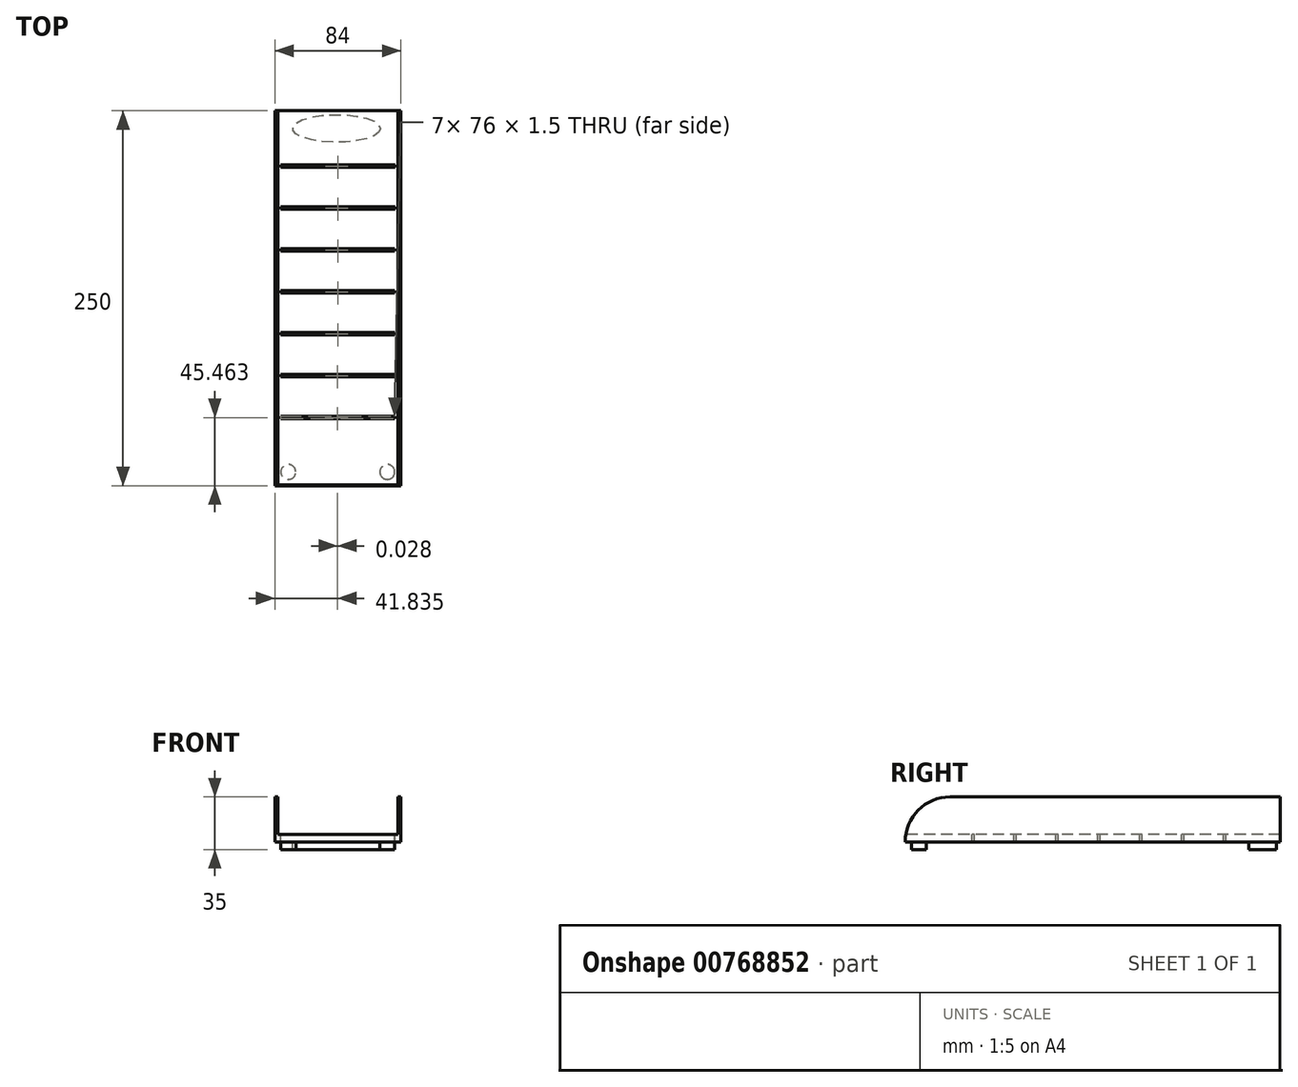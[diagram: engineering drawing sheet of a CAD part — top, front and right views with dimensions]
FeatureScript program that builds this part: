
annotation { "Feature Type Name" : "Feature", "Feature Type Description" : "" }
export const myFeature = defineFeature(function(context is Context, id is Id, definition is map)
    precondition{}
    {
        {
            var Q0;
            Q0=qCreatedBy(makeId("Front.planeOp"),FACE);
            var sketch = newSketch(context, id + "F0", { "sketchPlane" : qUnion([Q0])});
            skLineSegment(sketch, "E0.bottom", {"start": v(0, 0) * mm, "end": v(-84, 0) * mm});
            skLineSegment(sketch, "E0.top", {"start": v(0, 30) * mm, "end": v(-84, 30) * mm});
            skLineSegment(sketch, "E0.left", {"start": v(0, 0) * mm, "end": v(0, 30) * mm});
            skLineSegment(sketch, "E0.right", {"start": v(-84, 0) * mm, "end": v(-84, 30) * mm});
            skSolve(sketch);
        }
        {
            var Q0;
            Q0 = qSketchRegion(id + "F0", true);
            extrude(context, id + "F1", {"entities" : qUnion([Q0]), "oppositeDirection" : true, "depth" : 250 * mm, "offsetDistance" : 25.4 * mm});
        }
        {
            var Q0;
            Q0=qCreatedBy(makeId("Front.planeOp"),FACE);
            var sketch = newSketch(context, id + "F2", { "sketchPlane" : qUnion([Q0])});
            skLineSegment(sketch, "E1.bottom", {"start": v(-82, 55.6) * mm, "end": v(-2, 55.6) * mm});
            skLineSegment(sketch, "E1.top", {"start": v(-82, 5) * mm, "end": v(-2, 5) * mm});
            skLineSegment(sketch, "E1.left", {"start": v(-82, 55.6) * mm, "end": v(-82, 5) * mm});
            skLineSegment(sketch, "E1.right", {"start": v(-2, 55.6) * mm, "end": v(-2, 5) * mm});
            skSolve(sketch);
        }
        {
            var Q0;
            Q0=makeQuery(id+"F2.imprint","IMPRINT",FACE,{"disambiguationData":[TD([[makeQuery(id+"F2.imprint","IMPRINT",EDGE,{"derivedFrom":sQuery(id+"F2.wireOp",EDGE,"E1.bottom")}),-1.0]])]});
            extrude(context, id + "F3", {"entities" : qUnion([Q0]), "operationType" : NewBodyOperationType.REMOVE, "endBound" : BoundingType.THROUGH_ALL, "oppositeDirection" : true, "depth" : 25.4 * mm, "offsetDistance" : 25.4 * mm});
        }
        {
            var Q0;
            Q0=makeQuery(id+"F1.opExtrude","SWEPT_FACE",FACE,{"disambiguationData":[OSD([sQuery(id+"F0.wireOp",EDGE,"E0.bottom")])]});
            var sketch = newSketch(context, id + "F4", { "sketchPlane" : qUnion([Q0])});
            skCircle(sketch, "E2", {"center": v(-75.07, -9.18) * mm, "radius": 5 * mm});
            skEllipse(sketch, "E3", {"center": v(-42.93, -238.18) * mm, "majorRadius": 29.27 * mm, "minorRadius": 9.21 * mm, "majorAxis": v(1, 0)});
            skPoint(sketch, "E4.0.internal.snap0", {"position": v(-42, 0) * mm});
            skPoint(sketch, "E4.1.internal.snap0", {"position": v(-42, 0) * mm});
            skPoint(sketch, "E4.2.internal.snap0", {"position": v(-42, 0) * mm});
            skFitSpline(sketch, "E4", {"points": [v(-42, 9.43) * mm, v(-42, -255.98) * mm, v(-42, -257.6) * mm], "startDerivative": vector(0, -408.49) * mm, "endDerivative": vector(0, -12.81) * mm});
            skCircle(sketch, "E5.1.0.0", {"center": v(-9.07, -9.18) * mm, "radius": 5 * mm});
            skLineSegment(sketch, "E5.direction1", {"start": v(-75.07, -9.18) * mm, "end": v(-9.07, -9.18) * mm, "construction": true});
            skSolve(sketch);
        }
        {
            var Q0;
            Q0=makeQuery(id+"F4.imprint","IMPRINT",FACE,{"disambiguationData":[TD([[makeQuery(id+"F4.imprint","IMPRINT",EDGE,{"derivedFrom":sQuery(id+"F4.wireOp",EDGE,"E2")}),1.0]])]});
            var Q1;
            Q1=makeQuery(id+"F4.imprint","IMPRINT",FACE,{"disambiguationData":[TD([[makeQuery(id+"F4.imprint","IMPRINT",EDGE,{"derivedFrom":sQuery(id+"F4.wireOp",EDGE,"E5.1.0.0")}),1.0]])]});
            var Q2;
            {var subQ0=sQuery(id+"F4.wireOp",EDGE,"E4");var subQ1=sQuery(id+"F4.wireOp",EDGE,"E3");var subQ2=makeQuery(id+"F4.imprint","INTERSECT",VERTEX,{"disambiguationData":[OD(0.0)],"derivedFrom":[subQ1,subQ0]});Q2=makeQuery(id+"F4.imprint","IMPRINT",FACE,{"disambiguationData":[TD([[makeQuery(id+"F4.imprint","IMPRINT",EDGE,{"disambiguationData":[TD([[subQ2,-1.0]])],"derivedFrom":subQ1}),1.0]])]});}
            var Q3;
            {var subQ0=sQuery(id+"F4.wireOp",EDGE,"E4");var subQ1=sQuery(id+"F4.wireOp",EDGE,"E3");var subQ2=makeQuery(id+"F4.imprint","INTERSECT",VERTEX,{"disambiguationData":[OD(0.0)],"derivedFrom":[subQ1,subQ0]});Q3=makeQuery(id+"F4.imprint","IMPRINT",FACE,{"disambiguationData":[TD([[makeQuery(id+"F4.imprint","IMPRINT",EDGE,{"disambiguationData":[TD([[subQ2,1.0]])],"derivedFrom":subQ1}),1.0]])]});}
            extrude(context, id + "F5", {"entities" : qUnion([Q0, Q1, Q2, Q3]), "operationType" : NewBodyOperationType.ADD, "depth" : 5 * mm, "offsetDistance" : 25.4 * mm});
        }
        {
            var Q0;
            Q0=makeQuery(id+"F3.boolean.opBoolean","COPY",FACE,{"derivedFrom":makeQuery(id+"F3.opExtrude","SWEPT_FACE",FACE,{"disambiguationData":[OSD([sQuery(id+"F2.wireOp",EDGE,"E1.top")])]})});
            var sketch = newSketch(context, id + "F6", { "sketchPlane" : qUnion([Q0])});
            skLineSegment(sketch, "E6.bottom", {"start": v(-80, 213.85) * mm, "end": v(-4, 213.85) * mm});
            skLineSegment(sketch, "E6.top", {"start": v(-80, 212.35) * mm, "end": v(-4, 212.35) * mm});
            skLineSegment(sketch, "E6.left", {"start": v(-80, 213.85) * mm, "end": v(-80, 212.35) * mm});
            skLineSegment(sketch, "E6.right", {"start": v(-4, 213.85) * mm, "end": v(-4, 212.35) * mm});
            skLineSegment(sketch, "E7.0.1.0", {"start": v(-80.03, 184.41) * mm, "end": v(-4.03, 184.41) * mm});
            skLineSegment(sketch, "E7.0.1.1", {"start": v(-80.03, 185.91) * mm, "end": v(-4.03, 185.91) * mm});
            skLineSegment(sketch, "E7.0.1.2", {"start": v(-80.03, 185.91) * mm, "end": v(-80.03, 184.41) * mm});
            skLineSegment(sketch, "E7.0.1.3", {"start": v(-4.03, 185.91) * mm, "end": v(-4.03, 184.41) * mm});
            skLineSegment(sketch, "E7.0.2.0", {"start": v(-80.05, 156.47) * mm, "end": v(-4.05, 156.47) * mm});
            skLineSegment(sketch, "E7.0.2.1", {"start": v(-80.05, 157.97) * mm, "end": v(-4.05, 157.97) * mm});
            skLineSegment(sketch, "E7.0.2.2", {"start": v(-80.05, 157.97) * mm, "end": v(-80.05, 156.47) * mm});
            skLineSegment(sketch, "E7.0.2.3", {"start": v(-4.05, 157.97) * mm, "end": v(-4.05, 156.47) * mm});
            skLineSegment(sketch, "E7.0.3.0", {"start": v(-80.08, 128.53) * mm, "end": v(-4.08, 128.53) * mm});
            skLineSegment(sketch, "E7.0.3.1", {"start": v(-80.08, 130.03) * mm, "end": v(-4.08, 130.03) * mm});
            skLineSegment(sketch, "E7.0.3.2", {"start": v(-80.08, 130.03) * mm, "end": v(-80.08, 128.53) * mm});
            skLineSegment(sketch, "E7.0.3.3", {"start": v(-4.08, 130.03) * mm, "end": v(-4.08, 128.53) * mm});
            skLineSegment(sketch, "E7.0.4.0", {"start": v(-80.1, 100.6) * mm, "end": v(-4.1, 100.6) * mm});
            skLineSegment(sketch, "E7.0.4.1", {"start": v(-80.1, 102.1) * mm, "end": v(-4.1, 102.1) * mm});
            skLineSegment(sketch, "E7.0.4.2", {"start": v(-80.1, 102.1) * mm, "end": v(-80.1, 100.6) * mm});
            skLineSegment(sketch, "E7.0.4.3", {"start": v(-4.1, 102.1) * mm, "end": v(-4.1, 100.6) * mm});
            skLineSegment(sketch, "E7.0.5.0", {"start": v(-80.14, 72.65) * mm, "end": v(-4.14, 72.65) * mm});
            skLineSegment(sketch, "E7.0.5.1", {"start": v(-80.14, 74.15) * mm, "end": v(-4.14, 74.15) * mm});
            skLineSegment(sketch, "E7.0.5.2", {"start": v(-80.14, 74.15) * mm, "end": v(-80.14, 72.65) * mm});
            skLineSegment(sketch, "E7.0.5.3", {"start": v(-4.14, 74.15) * mm, "end": v(-4.14, 72.65) * mm});
            skLineSegment(sketch, "E7.0.6.0", {"start": v(-80.16, 44.71) * mm, "end": v(-4.16, 44.71) * mm});
            skLineSegment(sketch, "E7.0.6.1", {"start": v(-80.16, 46.21) * mm, "end": v(-4.16, 46.21) * mm});
            skLineSegment(sketch, "E7.0.6.2", {"start": v(-80.16, 46.21) * mm, "end": v(-80.16, 44.71) * mm});
            skLineSegment(sketch, "E7.0.6.3", {"start": v(-4.16, 46.21) * mm, "end": v(-4.16, 44.71) * mm});
            skLineSegment(sketch, "E7.direction1", {"start": v(-80, 212.35) * mm, "end": v(-54.6, 212.35) * mm, "construction": true});
            skLineSegment(sketch, "E7.direction2", {"start": v(-80, 212.35) * mm, "end": v(-80.03, 184.41) * mm, "construction": true});
            skSolve(sketch);
        }
        {
            var Q0;
            Q0=makeQuery(id+"F6.imprint","IMPRINT",FACE,{"disambiguationData":[TD([[makeQuery(id+"F6.imprint","IMPRINT",EDGE,{"derivedFrom":sQuery(id+"F6.wireOp",EDGE,"E6.bottom")}),-1.0]])]});
            var Q1;
            Q1=makeQuery(id+"F6.imprint","IMPRINT",FACE,{"disambiguationData":[TD([[makeQuery(id+"F6.imprint","IMPRINT",EDGE,{"derivedFrom":sQuery(id+"F6.wireOp",EDGE,"E7.0.1.0")}),1.0]])]});
            var Q2;
            Q2=makeQuery(id+"F6.imprint","IMPRINT",FACE,{"disambiguationData":[TD([[makeQuery(id+"F6.imprint","IMPRINT",EDGE,{"derivedFrom":sQuery(id+"F6.wireOp",EDGE,"E7.0.2.0")}),1.0]])]});
            var Q3;
            Q3=makeQuery(id+"F6.imprint","IMPRINT",FACE,{"disambiguationData":[TD([[makeQuery(id+"F6.imprint","IMPRINT",EDGE,{"derivedFrom":sQuery(id+"F6.wireOp",EDGE,"E7.0.6.0")}),1.0]])]});
            var Q4;
            Q4=makeQuery(id+"F6.imprint","IMPRINT",FACE,{"disambiguationData":[TD([[makeQuery(id+"F6.imprint","IMPRINT",EDGE,{"derivedFrom":sQuery(id+"F6.wireOp",EDGE,"E7.0.5.0")}),1.0]])]});
            var Q5;
            Q5=makeQuery(id+"F6.imprint","IMPRINT",FACE,{"disambiguationData":[TD([[makeQuery(id+"F6.imprint","IMPRINT",EDGE,{"derivedFrom":sQuery(id+"F6.wireOp",EDGE,"E7.0.4.0")}),1.0]])]});
            var Q6;
            Q6=makeQuery(id+"F6.imprint","IMPRINT",FACE,{"disambiguationData":[TD([[makeQuery(id+"F6.imprint","IMPRINT",EDGE,{"derivedFrom":sQuery(id+"F6.wireOp",EDGE,"E7.0.3.0")}),1.0]])]});
            extrude(context, id + "F7", {"entities" : qUnion([Q0, Q1, Q2, Q3, Q4, Q5, Q6]), "operationType" : NewBodyOperationType.REMOVE, "oppositeDirection" : true, "depth" : 25.4 * mm, "offsetDistance" : 25.4 * mm});
        }
        {
            var Q0;
            {var subQ0=sQuery(id+"F0.wireOp",EDGE,"E0.right");var subQ1=sQuery(id+"F0.wireOp",EDGE,"E0.top");Q0=makeQuery(id+"F3.boolean.opBoolean","SPLIT",EDGE,{"disambiguationData":[TD([makeQuery(id+"F1.opExtrude","SWEPT_FACE",FACE,{"disambiguationData":[OSD([subQ0])]})])],"derivedFrom":makeQuery(id+"F1.opExtrude","CAP_EDGE",EDGE,{"disambiguationData":[OSD([subQ1])],"isStart":true})});}
            var Q1;
            {var subQ0=sQuery(id+"F0.wireOp",EDGE,"E0.left");var subQ1=sQuery(id+"F0.wireOp",EDGE,"E0.top");Q1=makeQuery(id+"F3.boolean.opBoolean","SPLIT",EDGE,{"disambiguationData":[TD([makeQuery(id+"F1.opExtrude","SWEPT_FACE",FACE,{"disambiguationData":[OSD([subQ0])]})])],"derivedFrom":makeQuery(id+"F1.opExtrude","CAP_EDGE",EDGE,{"disambiguationData":[OSD([subQ1])],"isStart":true})});}
            fillet(context, id + "F8", {"entities" : qUnion([Q0, Q1]), "radius" : 30 * mm, "tangentPropagation" : true, "allowEdgeOverflow" : false});
        }
    });
